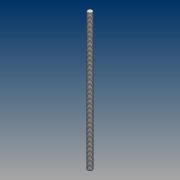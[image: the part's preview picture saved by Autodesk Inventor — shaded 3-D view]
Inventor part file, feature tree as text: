
AUTODESK INVENTOR PART (.ipt)
format: ipt  version: 2021 (Build 250183000, 183)  size: 2,712,064 bytes
history: native  units: mm
features: sketch x2, extrude x1, helix x1, projected_geometry x1
ambient origin geometry x8: Origin, YZ Plane, XZ Plane, XY Plane, X Axis, Y Axis, Z Axis, Center Point
bodies: Solid1 (feature_tree)
feature tree (5):
  extrude  "Extrusion1"  Depth=250.0mm TaperAngle=0.0deg
  helix  "Coil1"  [1 undecoded]
  sketch  "Sketch1"  dims[d0=8.0mm d1=250.0mm d2=0.0mm d3=0.2mm]
  sketch  "Sketch2"  dims[d4=0.45mm d5=2.0mm d6=250.0mm d7=10.0mm d8=0.0mm d9=90.0deg d10=90.0deg d11=0.0mm d12=0.0mm]
  projected_geometry  "Projected Loop1"
note: 1 required parameter value undecoded (feature->parameter linkage not recoverable at this tier; creation-order binding heuristic only, values carry confidence <= 0.55)
